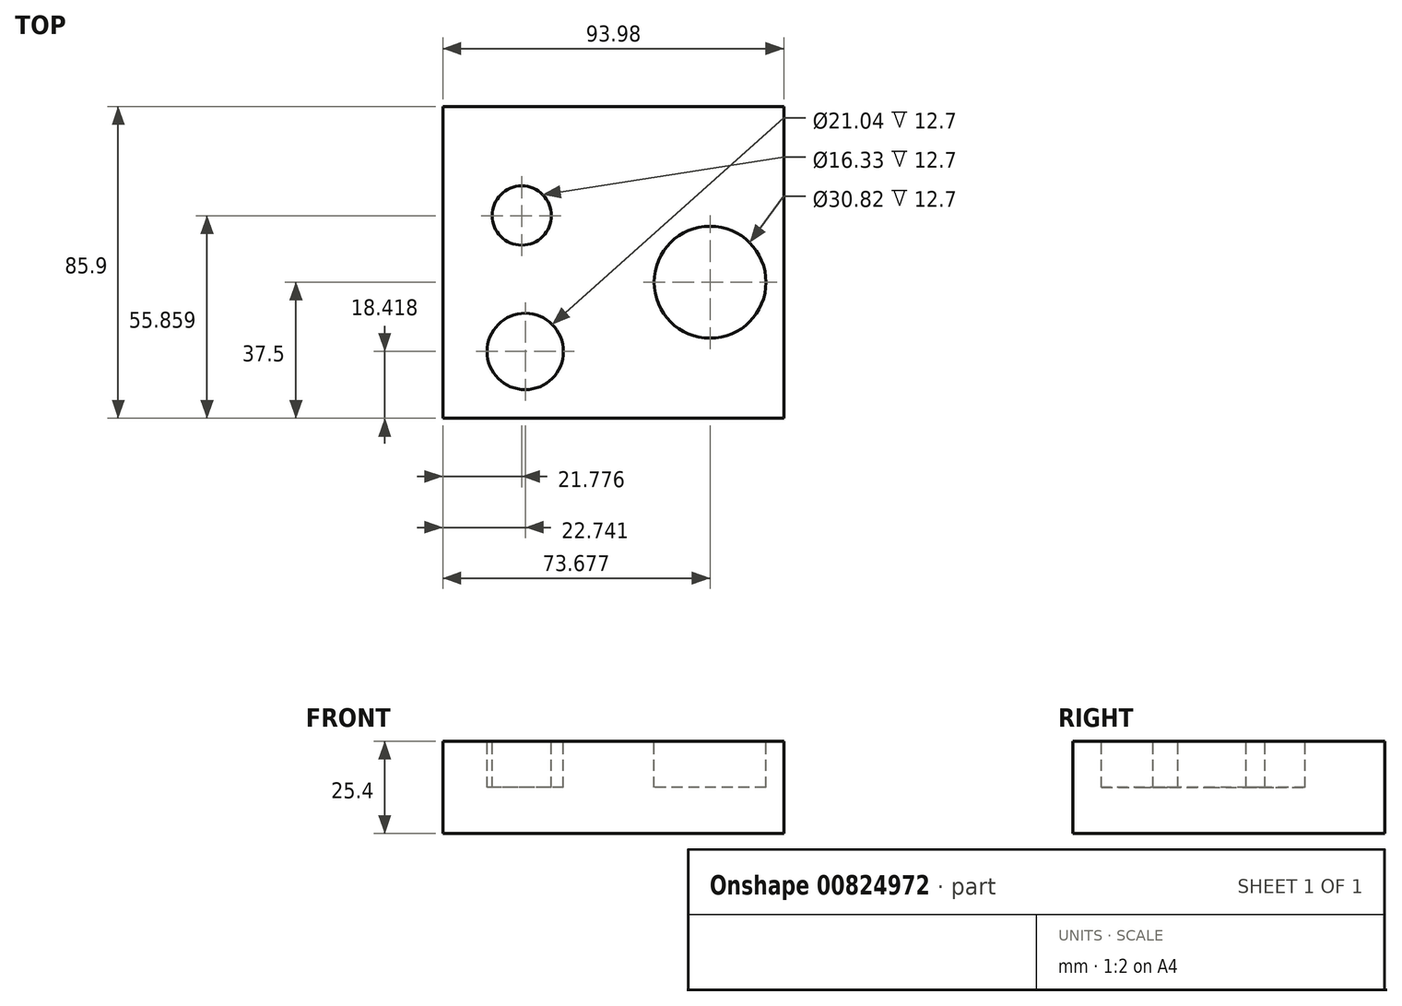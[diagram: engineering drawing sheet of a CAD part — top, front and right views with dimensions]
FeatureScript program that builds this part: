
annotation { "Feature Type Name" : "Feature", "Feature Type Description" : "" }
export const myFeature = defineFeature(function(context is Context, id is Id, definition is map)
    precondition{}
    {
        {
            var Q0;
            Q0=qCreatedBy(makeId("Top.planeOp"),FACE);
            var sketch = newSketch(context, id + "F0", { "sketchPlane" : qUnion([Q0])});
            skLineSegment(sketch, "E0.bottom", {"start": v(-46.99, -42.95) * mm, "end": v(46.99, -42.95) * mm});
            skLineSegment(sketch, "E0.top", {"start": v(-46.99, 42.95) * mm, "end": v(46.99, 42.95) * mm});
            skLineSegment(sketch, "E0.left", {"start": v(-46.99, -42.95) * mm, "end": v(-46.99, 42.95) * mm});
            skLineSegment(sketch, "E0.right", {"start": v(46.99, -42.95) * mm, "end": v(46.99, 42.95) * mm});
            skPoint(sketch, "E0.middle", {"position": v(0, 0) * mm});
            skSolve(sketch);
        }
        {
            var Q0;
            {var subQ0=sQuery(id+"F0.wireOp",EDGE,"btmygUUP-eZip-NsnF-6Hiv-op821y98u8FO");Q0=makeQuery(id+"F0.imprint","IMPRINT",FACE,{"disambiguationData":[TD([[makeQuery(id+"F0.imprint","IMPRINT",EDGE,{"derivedFrom":subQ0}),1.0]])]});}
            var Q1;
            Q1=makeQuery(id+"F0.imprint","IMPRINT",FACE,{"disambiguationData":[TD([[makeQuery(id+"F0.imprint","IMPRINT",EDGE,{"derivedFrom":sQuery(id+"F0.wireOp",EDGE,"E0.bottom")}),1.0]])]});
            extrude(context, id + "F1", {"entities" : qUnion([Q0, Q1]), "depth" : 25.4 * mm, "offsetDistance" : 25.4 * mm});
        }
        {
            var Q0;
            Q0=makeQuery(id+"F1.opExtrude","CAP_FACE",FACE,{"disambiguationData":[OSD([sQuery(id+"F0.wireOp",EDGE,"E0.bottom"),sQuery(id+"F0.wireOp",EDGE,"E0.top"),sQuery(id+"F0.wireOp",EDGE,"E0.left"),sQuery(id+"F0.wireOp",EDGE,"E0.right")])],"isStart":false});
            var sketch = newSketch(context, id + "F2", { "sketchPlane" : qUnion([Q0])});
            skCircle(sketch, "E1", {"center": v(-24.25, -24.53) * mm, "radius": 10.52 * mm});
            skCircle(sketch, "E2", {"center": v(-25.21, 12.9) * mm, "radius": 8.16 * mm});
            skCircle(sketch, "E3", {"center": v(26.69, -5.45) * mm, "radius": 15.4 * mm});
            skSolve(sketch);
        }
        {
            var Q0;
            Q0 = qSketchRegion(id + "F2", true);
            extrude(context, id + "F3", {"entities" : qUnion([Q0]), "operationType" : NewBodyOperationType.REMOVE, "oppositeDirection" : true, "depth" : 12.7 * mm, "offsetDistance" : 25.4 * mm});
        }
    });
